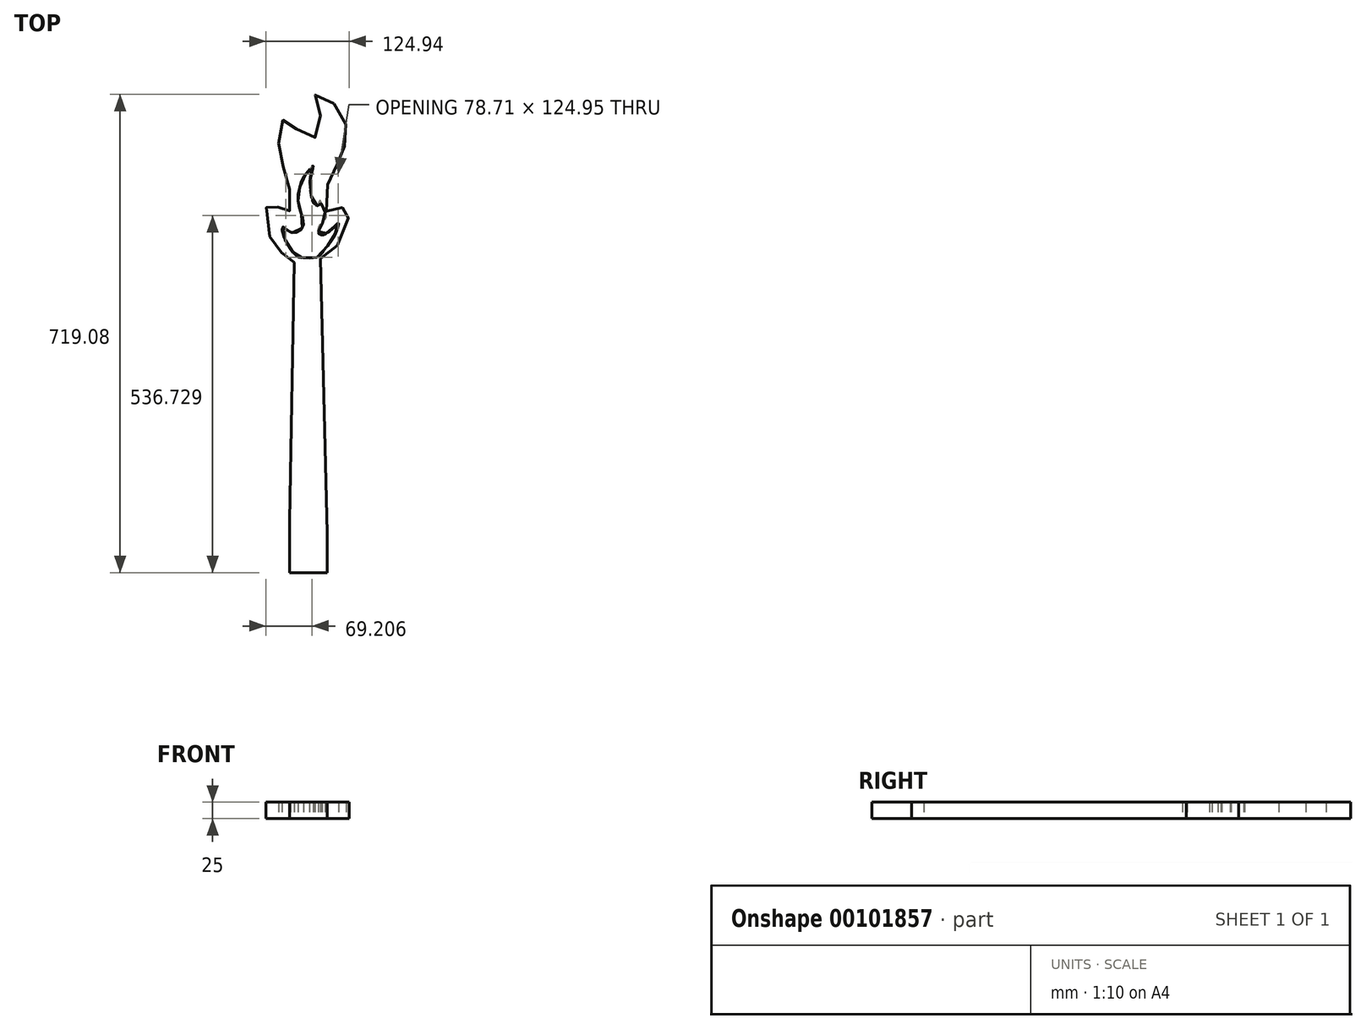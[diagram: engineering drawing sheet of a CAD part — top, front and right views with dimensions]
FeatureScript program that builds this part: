
annotation { "Feature Type Name" : "Feature", "Feature Type Description" : "" }
export const myFeature = defineFeature(function(context is Context, id is Id, definition is map)
    precondition{}
    {
        {
            var Q0;
            Q0=qCreatedBy(makeId("Top.planeOp"),FACE);
            var sketch = newSketch(context, id + "F0", { "sketchPlane" : qUnion([Q0])});
            skFitSpline(sketch, "E0", {"points": [v(20.03, 369.26) * mm, v(51.2, 398.9) * mm, v(59.77, 448.37) * mm, v(32.89, 437.1) * mm, v(31.56, 483.77) * mm, v(48.6, 517.67) * mm, v(58.56, 554.42) * mm, v(45.92, 596.86) * mm, v(12.02, 615.31) * mm, v(21.83, 570.04) * mm, v(0, 550.3) * mm, v(-31.88, 580.05) * mm, v(-43.25, 550.37) * mm, v(-33.45, 499.45) * mm, v(-25.05, 455.6) * mm, v(-32.16, 435.82) * mm, v(-56.16, 455.66) * mm, v(-57.67, 406.18) * mm, v(-36.52, 376.44) * mm, v(-19.57, 363.68) * mm, v(20.03, 369.26) * mm]});
            skLineSegment(sketch, "E1", {"start": v(-19.57, 363.68) * mm, "end": v(-26.78, -24.95) * mm});
            skLineSegment(sketch, "E2", {"start": v(20.03, 369.26) * mm, "end": v(29.78, -43.33) * mm});
            skLineSegment(sketch, "E3", {"start": v(-26.78, -24.95) * mm, "end": v(-26.78, -102.72) * mm});
            skLineSegment(sketch, "E4", {"start": v(-26.78, -102.72) * mm, "end": v(29.78, -102.72) * mm});
            skLineSegment(sketch, "E5", {"start": v(29.78, -102.72) * mm, "end": v(29.78, -43.33) * mm});
            skFitSpline(sketch, "E6", {"points": [v(14.79, 371.54) * mm, v(26.37, 383.64) * mm, v(37.42, 397.32) * mm, v(43.81, 410.9) * mm, v(46.98, 422.76) * mm, v(39.12, 415.42) * mm, v(28.5, 407.24) * mm, v(21.32, 404.79) * mm, v(16.78, 410.15) * mm, v(19.64, 421.6) * mm, v(21.42, 421.52) * mm, v(28.26, 430.81) * mm, v(27.2, 438.53) * mm, v(22.09, 443.53) * mm, v(22.14, 448.09) * mm, v(18.68, 457.16) * mm, v(16.08, 449.33) * mm, v(11.47, 450.16) * mm, v(6.21, 461.85) * mm, v(3.56, 476.16) * mm, v(4.88, 492.86) * mm, v(7.92, 504.43) * mm, v(8.68, 508.78) * mm, v(-4.5, 493.74) * mm, v(-9.6, 482.46) * mm, v(-13.66, 464.75) * mm, v(-13.38, 454.7) * mm, v(-11, 441.97) * mm, v(-6.01, 428.44) * mm, v(-7.9, 414.42) * mm, v(-16.33, 408.88) * mm, v(-26.1, 409.41) * mm, v(-33.6, 415.46) * mm, v(-37.4, 417.2) * mm, v(-35.38, 403.54) * mm, v(-28.23, 388.95) * mm, v(-18.4, 375.68) * mm, v(-12.6, 371.24) * mm, v(-3.09, 370.93) * mm, v(14.79, 371.54) * mm]});
            skSolve(sketch);
        }
        {
            var Q0;
            Q0=makeQuery(id+"F0.imprint","IMPRINT",FACE,{"disambiguationData":[TD([[makeQuery(id+"F0.imprint","IMPRINT",EDGE,{"derivedFrom":sQuery(id+"F0.wireOp",EDGE,"E6")}),-1.0]])]});
            var Q1;
            {var subQ0=sQuery(id+"F0.wireOp",EDGE,"E1");Q1=makeQuery(id+"F0.imprint","IMPRINT",FACE,{"disambiguationData":[TD([[makeQuery(id+"F0.imprint","IMPRINT",EDGE,{"derivedFrom":subQ0}),1.0]])]});}
            extrude(context, id + "F1", {"entities" : qUnion([Q0, Q1]), "depth" : 25 * mm});
        }
    });
